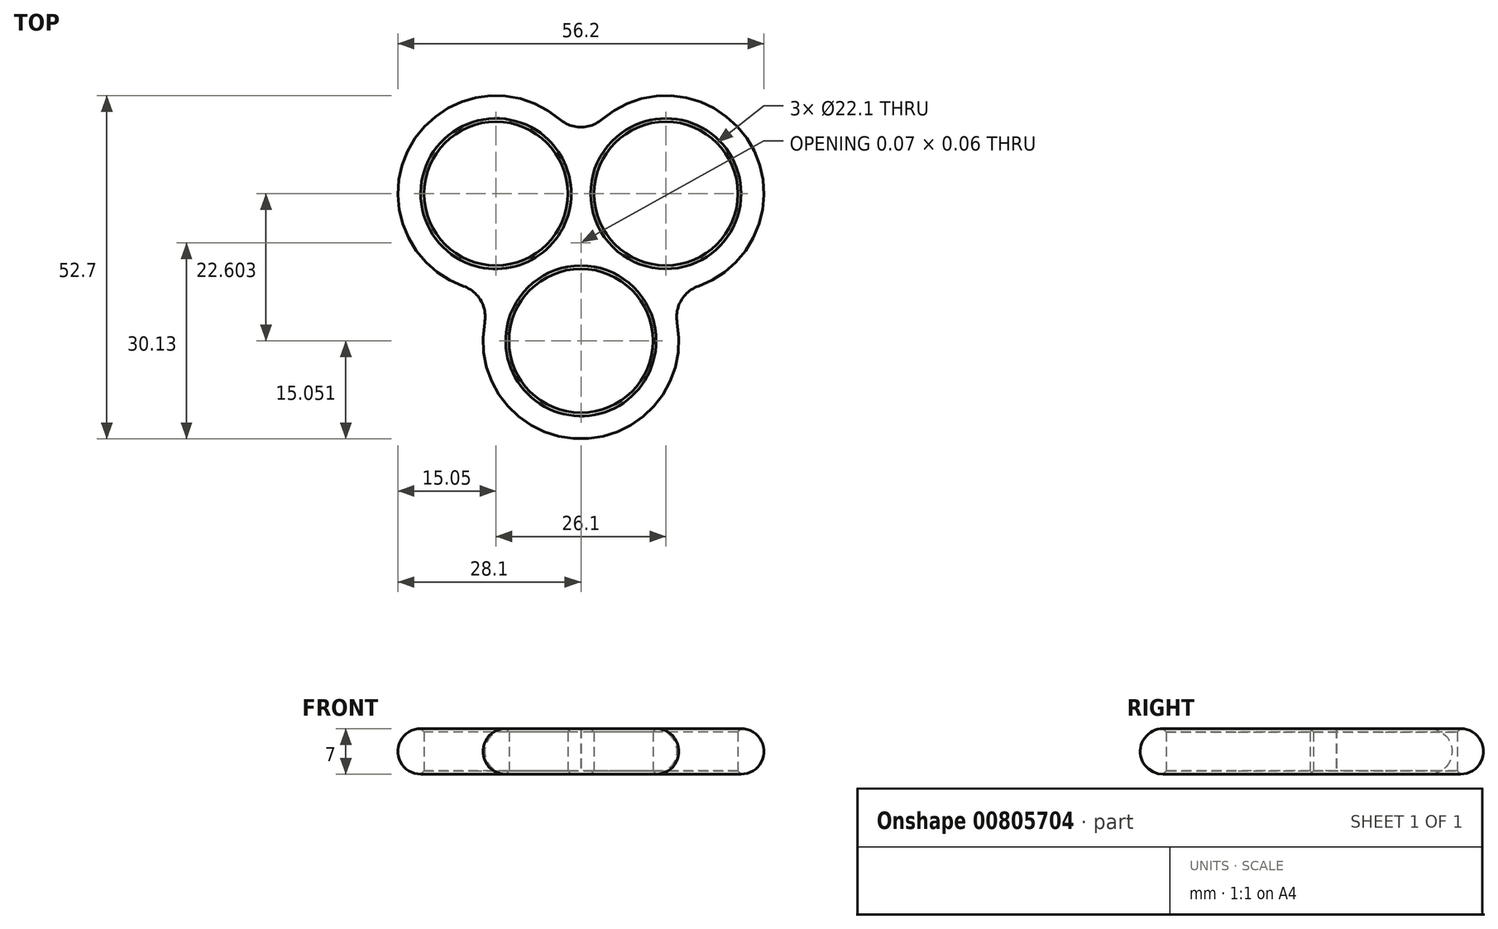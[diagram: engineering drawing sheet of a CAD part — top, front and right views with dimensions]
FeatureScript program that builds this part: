
annotation { "Feature Type Name" : "Feature", "Feature Type Description" : "" }
export const myFeature = defineFeature(function(context is Context, id is Id, definition is map)
    precondition{}
    {
        {
            var Q0;
            Q0=qCreatedBy(makeId("Top.planeOp"),FACE);
            var sketch = newSketch(context, id + "F0", { "sketchPlane" : qUnion([Q0])});
            skCircle(sketch, "E0", {"center": v(-13.05, 7.53) * mm, "radius": 11.05 * mm});
            skCircle(sketch, "E1", {"center": v(13.05, 7.53) * mm, "radius": 11.05 * mm});
            skCircle(sketch, "E2", {"center": v(0, -15.07) * mm, "radius": 11.05 * mm});
            skLineSegment(sketch, "E3", {"start": v(-13.05, 7.53) * mm, "end": v(13.05, 7.53) * mm, "construction": true});
            skLineSegment(sketch, "E4", {"start": v(13.05, 7.53) * mm, "end": v(0, -15.07) * mm, "construction": true});
            skLineSegment(sketch, "E5", {"start": v(0, -15.07) * mm, "end": v(-13.05, 7.53) * mm, "construction": true});
            skLineSegment(sketch, "E6", {"start": v(6.52, -3.77) * mm, "end": v(-13.05, 7.53) * mm, "construction": true});
            skArc(sketch, "E7", {"start": v(-3.25, 18.96) * mm, "mid": v(-26.08, 15.06) * mm, "end": v(-18.05, -6.66) * mm});
            skArc(sketch, "E8", {"start": v(18.05, -6.66) * mm, "mid": v(26.08, 15.06) * mm, "end": v(3.25, 18.96) * mm});
            skArc(sketch, "E9", {"start": v(0.03, -0.02) * mm, "mid": v(0, -0.02) * mm, "end": v(-0.03, -0.02) * mm});
            skArc(sketch, "E10.trimOffspring", {"start": v(0, 0.04) * mm, "mid": v(0.02, 0) * mm, "end": v(0.03, -0.02) * mm});
            skArc(sketch, "E11.trimOffspring", {"start": v(-14.8, -12.3) * mm, "mid": v(0, -30.12) * mm, "end": v(14.8, -12.3) * mm});
            skArc(sketch, "E12.trimOffspring", {"start": v(-0.03, -0.02) * mm, "mid": v(-0.02, 0) * mm, "end": v(0, 0.04) * mm});
            skPoint(sketch, "E13.visualSharp", {"position": v(0, 15.03) * mm});
            skArc(sketch, "E13.filletArc", {"start": v(-3.25, 18.96) * mm, "mid": v(0, 17.76) * mm, "end": v(3.25, 18.96) * mm});
            skPoint(sketch, "E14.visualSharp", {"position": v(13.02, -7.52) * mm});
            skArc(sketch, "E14.filletArc", {"start": v(18.05, -6.66) * mm, "mid": v(15.38, -8.88) * mm, "end": v(14.8, -12.3) * mm});
            skPoint(sketch, "E15.visualSharp", {"position": v(-13.02, -7.52) * mm});
            skArc(sketch, "E15.filletArc", {"start": v(-14.8, -12.3) * mm, "mid": v(-15.38, -8.88) * mm, "end": v(-18.05, -6.66) * mm});
            skSolve(sketch);
        }
        {
            var Q0;
            Q0=makeQuery(id+"F0.imprint","IMPRINT",FACE,{"disambiguationData":[TD([[makeQuery(id+"F0.imprint","IMPRINT",EDGE,{"derivedFrom":sQuery(id+"F0.wireOp",EDGE,"E0")}),-1.0]])]});
            extrude(context, id + "F1", {"entities" : qUnion([Q0]), "depth" : 7 * mm, "offsetDistance" : 25 * mm});
        }
        {
            var Q0;
            Q0=makeQuery(id+"F1.opExtrude","CAP_EDGE",EDGE,{"disambiguationData":[OSD([sQuery(id+"F0.wireOp",EDGE,"E14.filletArc")])],"isStart":false});
            var Q1;
            Q1=makeQuery(id+"F1.opExtrude","CAP_EDGE",EDGE,{"disambiguationData":[OSD([sQuery(id+"F0.wireOp",EDGE,"E14.filletArc")])],"isStart":true});
            fillet(context, id + "F2", {"entities" : qUnion([Q0, Q1]), "radius" : 3.5 * mm, "tangentPropagation" : true, "allowEdgeOverflow" : false});
        }
        {
            var Q0;
            Q0=makeQuery(id+"F1.opExtrude","CAP_EDGE",EDGE,{"disambiguationData":[OSD([sQuery(id+"F0.wireOp",EDGE,"E1")])],"isStart":false});
            var Q1;
            Q1=makeQuery(id+"F1.opExtrude","CAP_EDGE",EDGE,{"disambiguationData":[OSD([sQuery(id+"F0.wireOp",EDGE,"E1")])],"isStart":true});
            var Q2;
            Q2=makeQuery(id+"F1.opExtrude","CAP_EDGE",EDGE,{"disambiguationData":[OSD([sQuery(id+"F0.wireOp",EDGE,"E0")])],"isStart":true});
            var Q3;
            Q3=makeQuery(id+"F1.opExtrude","CAP_EDGE",EDGE,{"disambiguationData":[OSD([sQuery(id+"F0.wireOp",EDGE,"E0")])],"isStart":false});
            var Q4;
            Q4=makeQuery(id+"F1.opExtrude","CAP_EDGE",EDGE,{"disambiguationData":[OSD([sQuery(id+"F0.wireOp",EDGE,"E2")])],"isStart":false});
            var Q5;
            Q5=makeQuery(id+"F1.opExtrude","CAP_EDGE",EDGE,{"disambiguationData":[OSD([sQuery(id+"F0.wireOp",EDGE,"E2")])],"isStart":true});
            chamfer(context, id + "F3", {"entities" : qUnion([Q0, Q1, Q2, Q3, Q4, Q5]), "width" : .5 * mm, "tangentPropagation" : true});
        }
    });
